# Revit family: KOMFORT Roto EC DE 651-E
name_source: partatom
category: Mechanical Equipment
units: mm (PartAtom-declared; Revit-internal decimal feet)

## family parameters
Always vertical = Yes
Cut with Voids When Loaded = No
OmniClass Number = 23.75.00.00
OmniClass Title = Climate Control (HVAC)
Part Type = Normal
Room Calculation Point = No
Round Connector Dimension = Use Diameter
Shared = No
Work Plane-Based = No

## types (4) — shared parameters
00_20_Manufacturer = Blauberg
00_20_Name = Single-room air handling unit with heat recovery
A = 1240 mm  [stored 4.06824 ft]
A1 = 1340 mm  [stored 4.39633 ft]
A2 = 1190 mm  [stored 3.9042 ft]
B = 850 mm  [stored 2.78871 ft]
B1 = 906 mm  [stored 2.97244 ft]
B2 = 902 mm  [stored 2.95932 ft]
C = 199 mm  [stored 0.652887 ft]
C1 = 180 mm  [stored 0.590551 ft]
C2 = 435 mm  [stored 1.42717 ft]
C3 = 235 mm  [stored 0.770997 ft]
Casing Material = Polymer-coated steel (white)
D = 250 mm  [stored 0.82021 ft]
D1 = 123 mm  [stored 0.403543 ft]
D2 = 9 mm  [stored 0.0295276 ft]
E = 289 mm  [stored 0.948163 ft]
E1 = 410 mm  [stored 1.34514 ft]
Filter = G4
Frequency = 60 Hz
H = 425 mm  [stored 1.39436 ft]
Load Classification = HVAC
Maintenance zone material = <By Category>
Maximum Air Flow = 798.0 m³/h
Number of Fase = 1
Sound pressure level at 3 m distance = 31 dBA
Voltage = 230 V
b" = 26 mm
zero-valued in all types: Default Elevation

## per-type parameters (varying)
| type | 00_20_Type | Amperage | Power | Weight |
| KOMFORT Roto EC D 651 | KOMFORT Roto EC D 651 | 3 A | 377 W | 103.00 kg |
| KOMFORT Roto EC D 651-E | KOMFORT Roto EC D 651-E | 3 A | 377 W | 103.00 kg |
| KOMFORT Roto EC DE 651 | KOMFORT Roto EC DE 651 | 9 A | 1777 W | 104.00 kg |
| KOMFORT Roto EC DE 651-E | KOMFORT Roto EC DE 651 | 9 A | 1777 W | 104.00 kg |

note: [stored X ft] marks values corroborated as IEEE doubles in the binary element streams (Revit-internal decimal feet)

## geometry (parser evidence)
native form markers: Sweep x13
no freeform markers — native parametric forms only
